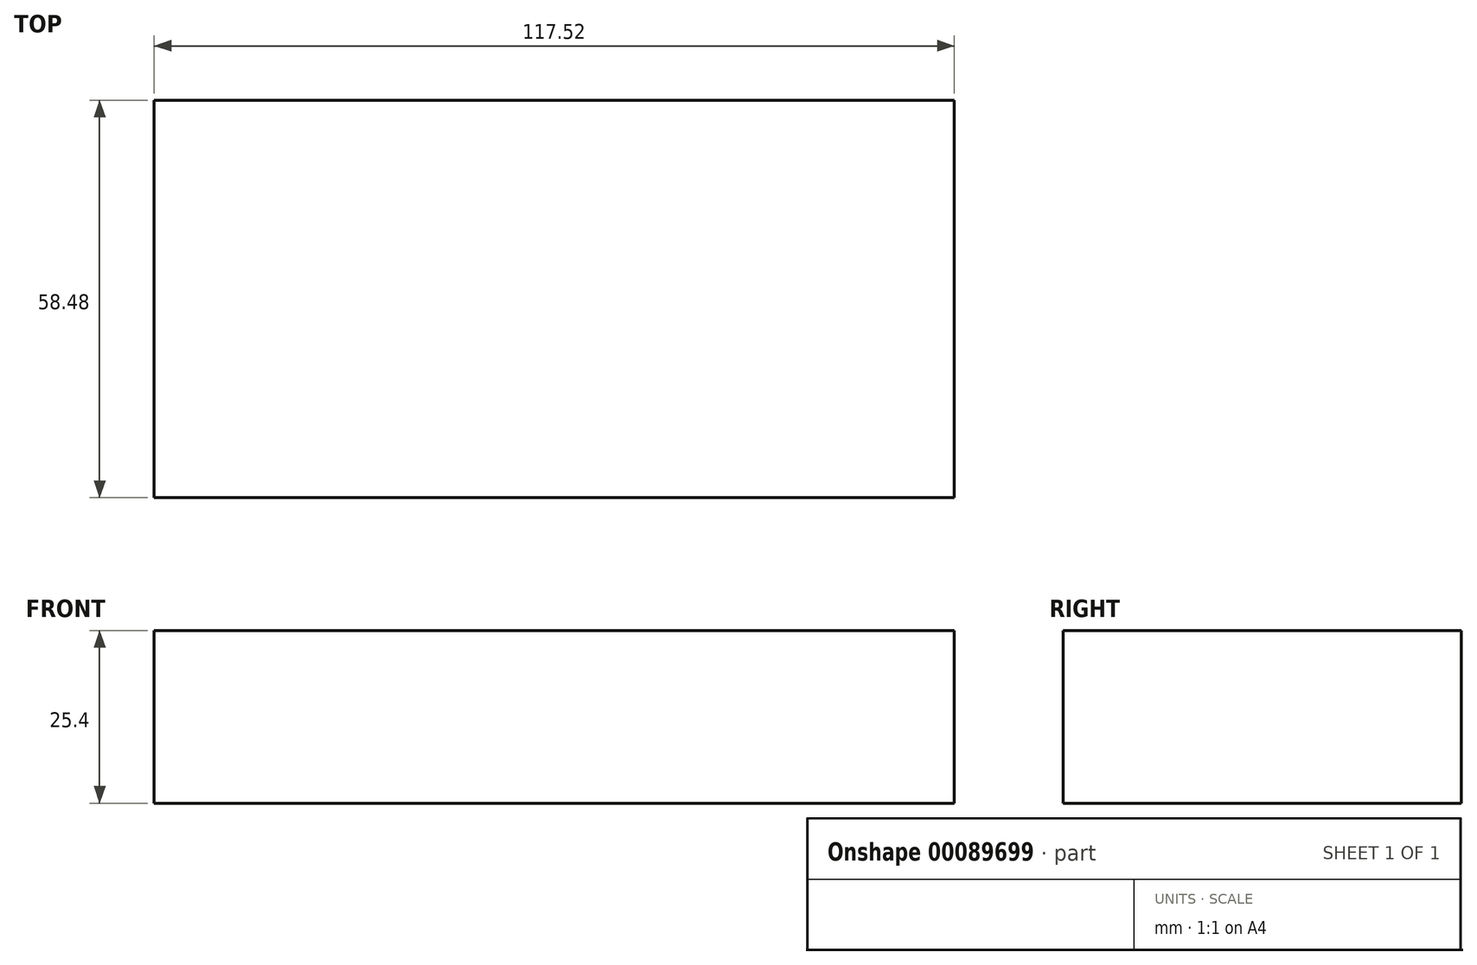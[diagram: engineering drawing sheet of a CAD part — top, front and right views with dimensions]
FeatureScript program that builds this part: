
annotation { "Feature Type Name" : "Feature", "Feature Type Description" : "" }
export const myFeature = defineFeature(function(context is Context, id is Id, definition is map)
    precondition{}
    {
        {
            var Q0;
            Q0=qCreatedBy(makeId("Top.planeOp"),FACE);
            var sketch = newSketch(context, id + "F0", { "sketchPlane" : qUnion([Q0])});
            skLineSegment(sketch, "E0.bottom", {"start": v(-58.76, 29.24) * mm, "end": v(58.76, 29.24) * mm});
            skLineSegment(sketch, "E0.top", {"start": v(-58.76, -29.24) * mm, "end": v(58.76, -29.24) * mm});
            skLineSegment(sketch, "E0.left", {"start": v(-58.76, 29.24) * mm, "end": v(-58.76, -29.24) * mm});
            skLineSegment(sketch, "E0.right", {"start": v(58.76, 29.24) * mm, "end": v(58.76, -29.24) * mm});
            skPoint(sketch, "E0.middle", {"position": v(0, 0) * mm});
            skPoint(sketch, "E1", {"position": v(-41.65, 0) * mm});
            skPoint(sketch, "E2", {"position": v(38.5, 0) * mm});
            skSolve(sketch);
        }
        {
            var Q0;
            Q0 = qSketchRegion(id + "F0", true);
            extrude(context, id + "F1", {"entities" : qUnion([Q0]), "depth" : 25.4 * mm});
        }
    });
